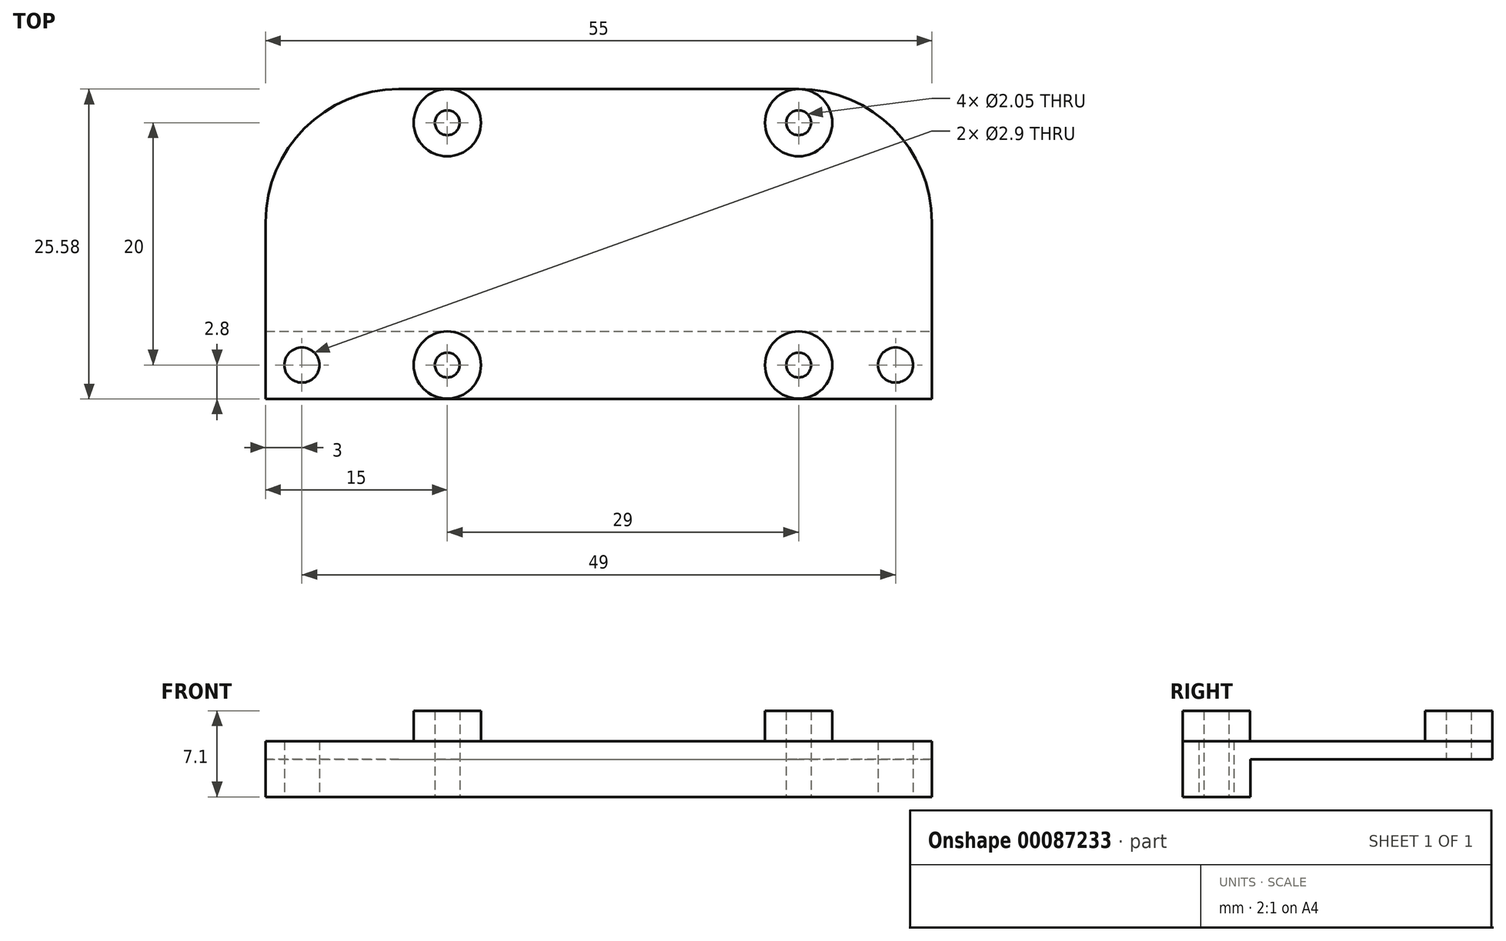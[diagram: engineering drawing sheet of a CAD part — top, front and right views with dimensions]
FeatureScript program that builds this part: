
annotation { "Feature Type Name" : "Feature", "Feature Type Description" : "" }
export const myFeature = defineFeature(function(context is Context, id is Id, definition is map)
    precondition{}
    {
        {
            var Q0;
            Q0=qCreatedBy(makeId("Top.planeOp"),FACE);
            var sketch = newSketch(context, id + "F0", { "sketchPlane" : qUnion([Q0])});
            skPoint(sketch, "E0.middle", {"position": v(0, 0) * mm});
            skCircle(sketch, "E1", {"center": v(-24.5, 0) * mm, "radius": 1.45 * mm});
            skCircle(sketch, "E2.MirrorC", {"center": v(24.5, 0) * mm, "radius": 1.45 * mm});
            skLineSegment(sketch, "E3.bottom", {"start": v(-27.5, -2.8) * mm, "end": v(27.5, -2.8) * mm});
            skLineSegment(sketch, "E3.top", {"start": v(-16.5, 22.77) * mm, "end": v(16.5, 22.77) * mm});
            skLineSegment(sketch, "E3.left", {"start": v(-27.5, -2.8) * mm, "end": v(-27.5, 11.77) * mm});
            skLineSegment(sketch, "E3.right", {"start": v(27.5, -2.8) * mm, "end": v(27.5, 11.78) * mm});
            skCircle(sketch, "E4", {"center": v(16.5, 0) * mm, "radius": 1.02 * mm});
            skPoint(sketch, "E5.visualSharp", {"position": v(-27.5, 22.77) * mm});
            skArc(sketch, "E5.filletArc", {"start": v(-16.5, 22.77) * mm, "mid": v(-24.28, 19.55) * mm, "end": v(-27.5, 11.77) * mm});
            skPoint(sketch, "E6.visualSharp", {"position": v(27.5, 22.77) * mm});
            skArc(sketch, "E6.filletArc", {"start": v(27.5, 11.78) * mm, "mid": v(24.28, 19.55) * mm, "end": v(16.5, 22.77) * mm});
            skCircle(sketch, "E7.0", {"center": v(16.5, 0) * mm, "radius": 2.77 * mm});
            skCircle(sketch, "E8.0.1.0", {"center": v(16.5, 20) * mm, "radius": 1.02 * mm});
            skCircle(sketch, "E8.0.1.1", {"center": v(16.5, 20) * mm, "radius": 2.77 * mm});
            skCircle(sketch, "E8.1.0.0", {"center": v(-12.5, 0) * mm, "radius": 1.02 * mm});
            skCircle(sketch, "E8.1.0.1", {"center": v(-12.5, 0) * mm, "radius": 2.77 * mm});
            skCircle(sketch, "E8.1.1.0", {"center": v(-12.5, 20) * mm, "radius": 1.02 * mm});
            skCircle(sketch, "E8.1.1.1", {"center": v(-12.5, 20) * mm, "radius": 2.77 * mm});
            skLineSegment(sketch, "E8.direction1", {"start": v(16.5, 0) * mm, "end": v(-12.5, 0) * mm, "construction": true});
            skLineSegment(sketch, "E8.direction2", {"start": v(16.5, 0) * mm, "end": v(16.5, 20) * mm, "construction": true});
            skLineSegment(sketch, "E9.MirrorCS", {"start": v(-27.5, 2.8) * mm, "end": v(27.5, 2.8) * mm});
            skSolve(sketch);
        }
        {
            var Q0;
            Q0=makeQuery(id+"F0.imprint","IMPRINT",FACE,{"disambiguationData":[TD([[makeQuery(id+"F0.imprint","IMPRINT",EDGE,{"derivedFrom":sQuery(id+"F0.wireOp",EDGE,"E1")}),-1.0]])]});
            var Q1;
            {var subQ3=sQuery(id+"F0.wireOp",EDGE,"E5.filletArc");Q1=makeQuery(id+"F0.imprint","IMPRINT",FACE,{"disambiguationData":[TD([[makeQuery(id+"F0.imprint","IMPRINT",EDGE,{"derivedFrom":subQ3}),1.0]])]});}
            var Q2;
            Q2=makeQuery(id+"F0.imprint","IMPRINT",FACE,{"disambiguationData":[TD([[makeQuery(id+"F0.imprint","IMPRINT",EDGE,{"derivedFrom":sQuery(id+"F0.wireOp",EDGE,"E8.0.1.0")}),-1.0]])]});
            var Q3;
            Q3=makeQuery(id+"F0.imprint","IMPRINT",FACE,{"disambiguationData":[TD([[makeQuery(id+"F0.imprint","IMPRINT",EDGE,{"derivedFrom":sQuery(id+"F0.wireOp",EDGE,"E8.1.1.0")}),-1.0]])]});
            var Q4;
            Q4=makeQuery(id+"F0.imprint","IMPRINT",FACE,{"disambiguationData":[TD([[makeQuery(id+"F0.imprint","IMPRINT",EDGE,{"derivedFrom":sQuery(id+"F0.wireOp",EDGE,"E4")}),-1.0]])]});
            var Q5;
            Q5=makeQuery(id+"F0.imprint","IMPRINT",FACE,{"disambiguationData":[TD([[makeQuery(id+"F0.imprint","IMPRINT",EDGE,{"derivedFrom":sQuery(id+"F0.wireOp",EDGE,"E8.1.0.0")}),-1.0]])]});
            extrude(context, id + "F1", {"entities" : qUnion([Q0, Q1, Q2, Q3, Q4, Q5]), "depth" : 1.5 * mm});
        }
        {
            var Q0;
            Q0=makeQuery(id+"F0.imprint","IMPRINT",FACE,{"disambiguationData":[TD([[makeQuery(id+"F0.imprint","IMPRINT",EDGE,{"derivedFrom":sQuery(id+"F0.wireOp",EDGE,"E1")}),-1.0]])]});
            var Q1;
            Q1=makeQuery(id+"F0.imprint","IMPRINT",FACE,{"disambiguationData":[TD([[makeQuery(id+"F0.imprint","IMPRINT",EDGE,{"derivedFrom":sQuery(id+"F0.wireOp",EDGE,"E8.1.0.0")}),-1.0]])]});
            var Q2;
            Q2=makeQuery(id+"F0.imprint","IMPRINT",FACE,{"disambiguationData":[TD([[makeQuery(id+"F0.imprint","IMPRINT",EDGE,{"derivedFrom":sQuery(id+"F0.wireOp",EDGE,"E4")}),-1.0]])]});
            extrude(context, id + "F2", {"entities" : qUnion([Q0, Q1, Q2]), "operationType" : NewBodyOperationType.ADD, "oppositeDirection" : true, "depth" : 3.1 * mm});
        }
        {
            var Q0;
            Q0=makeQuery(id+"F0.imprint","IMPRINT",FACE,{"disambiguationData":[TD([[makeQuery(id+"F0.imprint","IMPRINT",EDGE,{"derivedFrom":sQuery(id+"F0.wireOp",EDGE,"E8.0.1.0")}),-1.0]])]});
            var Q1;
            Q1=makeQuery(id+"F0.imprint","IMPRINT",FACE,{"disambiguationData":[TD([[makeQuery(id+"F0.imprint","IMPRINT",EDGE,{"derivedFrom":sQuery(id+"F0.wireOp",EDGE,"E8.1.1.0")}),-1.0]])]});
            var Q2;
            Q2=makeQuery(id+"F0.imprint","IMPRINT",FACE,{"disambiguationData":[TD([[makeQuery(id+"F0.imprint","IMPRINT",EDGE,{"derivedFrom":sQuery(id+"F0.wireOp",EDGE,"E4")}),-1.0]])]});
            var Q3;
            Q3=makeQuery(id+"F0.imprint","IMPRINT",FACE,{"disambiguationData":[TD([[makeQuery(id+"F0.imprint","IMPRINT",EDGE,{"derivedFrom":sQuery(id+"F0.wireOp",EDGE,"E8.1.0.0")}),-1.0]])]});
            extrude(context, id + "F3", {"entities" : qUnion([Q0, Q1, Q2, Q3]), "operationType" : NewBodyOperationType.ADD, "depth" : 4 * mm});
        }
    });
